# Revit family: streetlight_sl_11_iq_micro___st1_2a_5xc1a21f08de_154d
name_source: partatom
category: Lighting Fixtures
units: mm (PartAtom-declared; Revit-internal decimal feet)

## family parameters
Cut with Voids When Loaded = No
Host = Face
Light Source = No
Part Type = Normal
Room Calculation Point = No
Round Connector Dimension = Use Diameter
Shared = No

## types (1)
- --- (1 x LED, 3040 lm, 25.6 W, 2200K)
    Apparent Load = 26 VA
    CIE Flux Codes = 33 71 96 100 100
    Color Rendering = 70
    Color Temperature = 2200K
    Default Elevation = 1800 mm
    Description = Streetlight SL 11 iQ micro, mast luminaire, primary light control with 3 zone facetted reflector, of plastic, silver coated, highly specular, primary optical cover: cover, of PMMA, transparent, light distribution: ST1.2a, light emission: direct distribution, primary light characteristic: asymmetric, installation type: post-top, side-entry, LED, High Power LED, rated luminous flux: 3.070lm, luminous efficacy: 120lm/W, light colour: 722, colour temperature: 2200K, control: Street-Remote, optimised constant luminous flux control (CLO 2.0), Desk-Remote (wireless, voltage-free reading and setting of iQ features in the workshop via application-optimized NFC function/RFID function), Light-Fading, Smart-Wire, Night-Set, Lumen-Switch, Temp-Guard, Auto-Match, with cable H07RN-F 5x 1.5mm², mains connection: 220..240V, AC, 50/60Hz, connection cable pre-assembled, cable length: 6,5m, start of lifetime: 26W, end of lifetime: 26W, reduction: 12W, luminaire housing, of diecast aluminium, powder-coated, Siteco® metallic grey (DB 702S), length: 600mm, width: 174mm, height: 116mm, spigot size: 60/76mm (post-top) and 42/60/76mm (side-entry), mast flange for spigot size: 42mm: 5XC10008XM4, 60mm: 5XC10008XM2, 76/60mm: 5XC10108XM1, equipment: Power, protection rating (complete): IP66, insulation class (complete): insulation class II (safety insulation), certification: CE, ENEC, VDE, impact resistance: IK09, permissible operating ambient temperature for outdoor applications: -25..+50°C, standard-compliant lighting for roads and squares, packaging unit: 1 piece

Light Distribution: ST1.2a
    Height = 116 mm
    Lamp = 1 x LED
    Lamp Light Flux = 3040 lm
    Lamp Power = 25.6 W
    Lamp count = 1
    Length = 600 mm
    Luminous efficacy = 119 lm/W
    Manufacturer = Siteco
    ModVariant = No
    Model = 5XC1A21F08DE
    Number of Poles = 1
    OnlyDefault = Yes
    Power Factor = 1
    Product Name = Streetlight SL 11 iQ micro | ST1.2a
    Product group = mast luminaire | pylon top
    ProductGroupID = 6100
    Protection Class = Protection class II
    Protection Degree = IP 66
    RLX_Detail_Level = 1
    RlxData = <blob elided: 49857 chars, md5=bbf27112>
    Socket = socket
    Standby Power = 0 W
    System Light Flux = 3040 lm
    System Power = 26 W
    Type Comments = factory setting: luminous flux: 100 % | dim-lin: 254 | 478 mA
    Type Image = l_1006566.jpg
    URL = http://relux.com
    VarID = @adj_040073
    Voltage = 0 V
    Weight = 0.00 kg
    Width = 174 mm

## geometry (parser evidence)
native form markers: Sweep x9
no freeform markers — native parametric forms only
